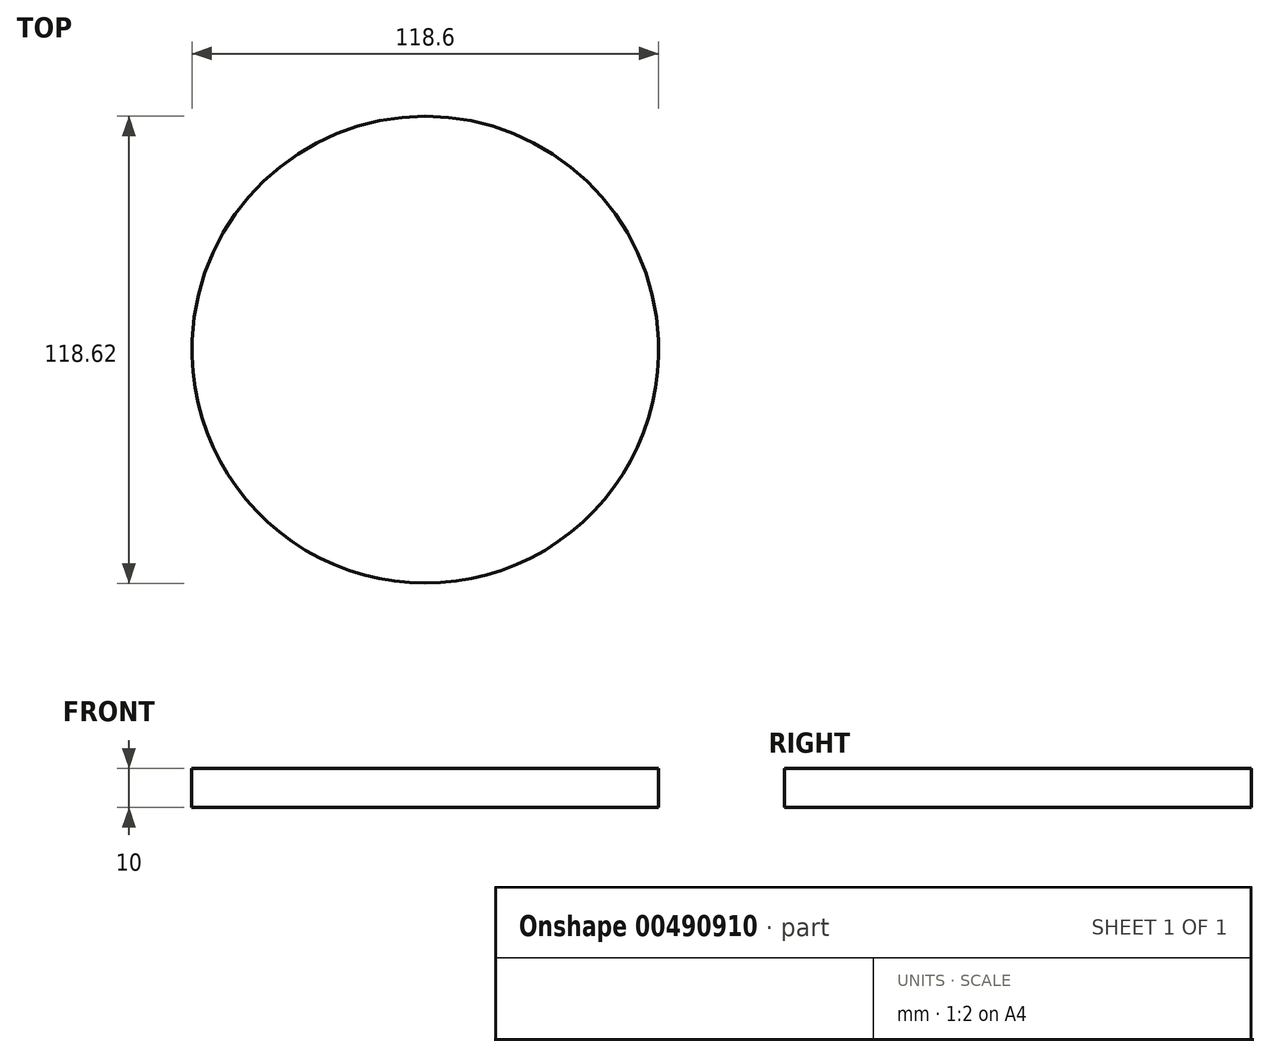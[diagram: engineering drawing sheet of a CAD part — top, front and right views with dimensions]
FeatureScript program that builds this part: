
annotation { "Feature Type Name" : "Feature", "Feature Type Description" : "" }
export const myFeature = defineFeature(function(context is Context, id is Id, definition is map)
    precondition{}
    {
        {
            var Q0;
            Q0=qCreatedBy(makeId("Top.planeOp"),FACE);
            var sketch = newSketch(context, id + "F0", { "sketchPlane" : qUnion([Q0])});
            skArc(sketch, "E0", {"start": v(60.37, 0) * mm, "mid": v(1.12, 56.83) * mm, "end": v(-58.13, 0) * mm});
            skArc(sketch, "E1", {"start": v(-58.13, 0) * mm, "mid": v(1.12, -61.8) * mm, "end": v(60.37, 0) * mm});
            skSolve(sketch);
        }
        {
            var Q0;
            Q0=makeQuery(id+"F0.imprint","IMPRINT",FACE,{"disambiguationData":[TD([[makeQuery(id+"F0.imprint","IMPRINT",EDGE,{"derivedFrom":sQuery(id+"F0.wireOp",EDGE,"E0")}),1.0]])]});
            extrude(context, id + "F1", {"entities" : qUnion([Q0]), "depth" : 10 * mm});
        }
        {
            var Q0;
            Q0=makeQuery(id+"F1.opExtrude","CAP_FACE",FACE,{"disambiguationData":[OSD([sQuery(id+"F0.wireOp",EDGE,"E0"),sQuery(id+"F0.wireOp",EDGE,"E1")])],"isStart":false});
            var sketch = newSketch(context, id + "F2", { "sketchPlane" : qUnion([Q0])});
            skArc(sketch, "E2", {"start": v(-22.24, 14.63) * mm, "mid": v(-30.7, 23.12) * mm, "end": v(-38.96, 14.43) * mm});
            skArc(sketch, "E3", {"start": v(-38.96, 14.43) * mm, "mid": v(-30.5, 5.72) * mm, "end": v(-22.24, 14.63) * mm});
            skArc(sketch, "E4", {"start": v(30.56, 14.63) * mm, "mid": v(21.68, 23.44) * mm, "end": v(12.8, 14.63) * mm});
            skArc(sketch, "E5", {"start": v(12.8, 14.63) * mm, "mid": v(21.68, 5.7) * mm, "end": v(30.56, 14.63) * mm});
            skSolve(sketch);
        }
    });
